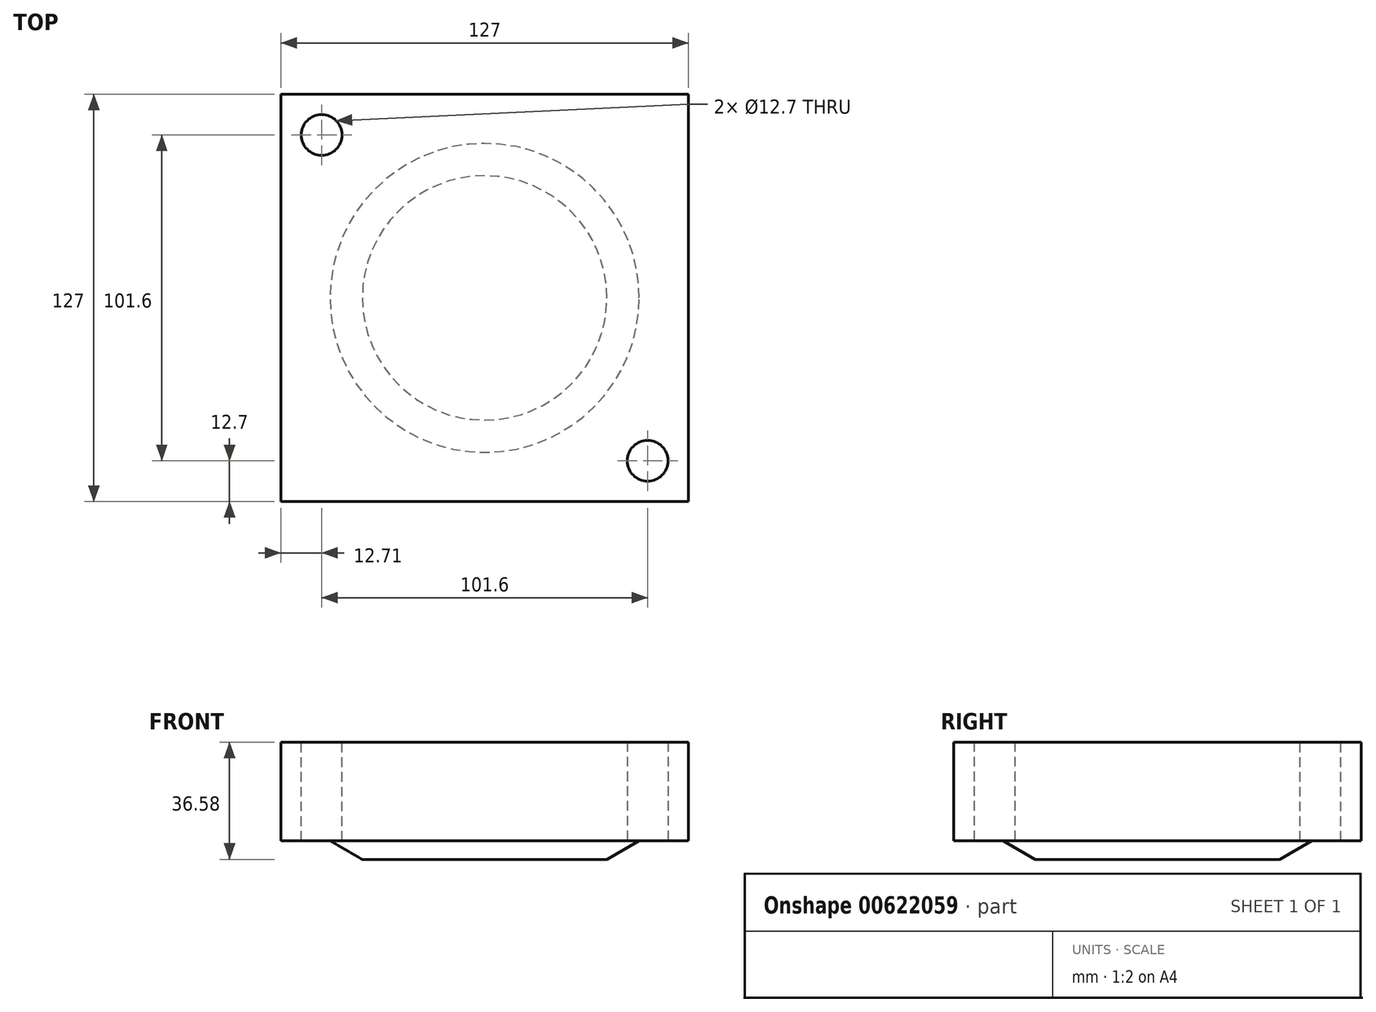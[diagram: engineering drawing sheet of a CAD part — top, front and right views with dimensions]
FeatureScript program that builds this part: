
annotation { "Feature Type Name" : "Feature", "Feature Type Description" : "" }
export const myFeature = defineFeature(function(context is Context, id is Id, definition is map)
    precondition{}
    {
        {
            var Q0;
            Q0=qCreatedBy(makeId("Front.planeOp"),FACE);
            var sketch = newSketch(context, id + "F0", { "sketchPlane" : qUnion([Q0])});
            skLineSegment(sketch, "E0", {"start": v(38.1, 1.52) * mm, "end": v(0, 1.52) * mm});
            skLineSegment(sketch, "E1", {"start": v(0, 1.52) * mm, "end": v(0, 0) * mm});
            skLineSegment(sketch, "E2", {"start": v(38.1, 1.52) * mm, "end": v(48.16, 7.33) * mm});
            skPoint(sketch, "E3.middle", {"position": v(0, 1.52) * mm});
            skLineSegment(sketch, "E4", {"start": v(0, 1.52) * mm, "end": v(38.1, 1.52) * mm});
            skLineSegment(sketch, "E5", {"start": v(48.16, 7.33) * mm, "end": v(92.57, 7.33) * mm});
            skLineSegment(sketch, "E6", {"start": v(92.57, 7.33) * mm, "end": v(92.57, 0) * mm});
            skLineSegment(sketch, "E7", {"start": v(0, 0) * mm, "end": v(92.57, 0) * mm});
            skSolve(sketch);
        }
        {
            var Q0;
            Q0=qCreatedBy(makeId("Front.planeOp"),FACE);
            var sketch = newSketch(context, id + "F1", { "sketchPlane" : qUnion([Q0])});
            skLineSegment(sketch, "E8.bottom", {"start": v(-63.5, 0) * mm, "end": v(63.5, 0) * mm});
            skLineSegment(sketch, "E8.top", {"start": v(-63.5, 38.1) * mm, "end": v(63.5, 38.1) * mm});
            skLineSegment(sketch, "E8.left", {"start": v(-63.5, 0) * mm, "end": v(-63.5, 38.1) * mm});
            skLineSegment(sketch, "E8.right", {"start": v(63.5, 0) * mm, "end": v(63.5, 38.1) * mm});
            skSolve(sketch);
        }
        {
            var Q0;
            Q0=makeQuery(id+"F1.imprint","IMPRINT",FACE,{"disambiguationData":[TD([[makeQuery(id+"F1.imprint","IMPRINT",EDGE,{"derivedFrom":sQuery(id+"F1.wireOp",EDGE,"E8.bottom")}),1.0]])]});
            extrude(context, id + "F2", {"entities" : qUnion([Q0]), "endBound" : BoundingType.SYMMETRIC, "depth" : 127 * mm, "offsetDistance" : 25.4 * mm});
        }
        {
            var Q0;
            Q0=makeQuery(id+"F0.imprint","IMPRINT",FACE,{"disambiguationData":[TD([[makeQuery(id+"F0.imprint","IMPRINT",EDGE,{"derivedFrom":sQuery(id+"F0.wireOp",EDGE,"E1")}),1.0]])]});
            var Q1;
            Q1=sQuery(id+"F0.wireOp",EDGE,"E1");
            revolve(context, id + "F3", {"operationType" : NewBodyOperationType.REMOVE, "entities" : qUnion([Q0]), "axis" : qUnion([Q1]), "revolveType" : RevolveType.FULL, "oppositeDirection" : true});
        }
        {
            var Q0;
            Q0=qCreatedBy(makeId("Top.planeOp"),FACE);
            var sketch = newSketch(context, id + "F4", { "sketchPlane" : qUnion([Q0])});
            skLineSegment(sketch, "E9", {"start": v(-50.8, 50.8) * mm, "end": v(0, 50.8) * mm});
            skLineSegment(sketch, "E10", {"start": v(-50.8, 50.8) * mm, "end": v(-50.8, 0) * mm});
            skCircle(sketch, "E11", {"center": v(-50.8, 50.8) * mm, "radius": 6.35 * mm});
            skSolve(sketch);
        }
        {
            var Q0;
            Q0 = qSketchRegion(id + "F4", true);
            extrude(context, id + "F5", {"entities" : qUnion([Q0]), "operationType" : NewBodyOperationType.REMOVE, "endBound" : BoundingType.SYMMETRIC, "oppositeDirection" : true, "depth" : 101.6 * mm, "offsetDistance" : 25.4 * mm});
        }
        {
            var Q0;
            Q0=qCreatedBy(makeId("Top.planeOp"),FACE);
            var sketch = newSketch(context, id + "F6", { "sketchPlane" : qUnion([Q0])});
            skLineSegment(sketch, "E12", {"start": v(0, -50.8) * mm, "end": v(50.8, -50.8) * mm});
            skLineSegment(sketch, "E13", {"start": v(50.8, -50.8) * mm, "end": v(50.8, 0) * mm});
            skCircle(sketch, "E14", {"center": v(50.8, -50.8) * mm, "radius": 6.35 * mm});
            skSolve(sketch);
        }
        {
            var Q0;
            Q0 = qSketchRegion(id + "F6", true);
            extrude(context, id + "F7", {"entities" : qUnion([Q0]), "operationType" : NewBodyOperationType.REMOVE, "endBound" : BoundingType.SYMMETRIC, "depth" : 101.6 * mm, "offsetDistance" : 25.4 * mm});
        }
    });
